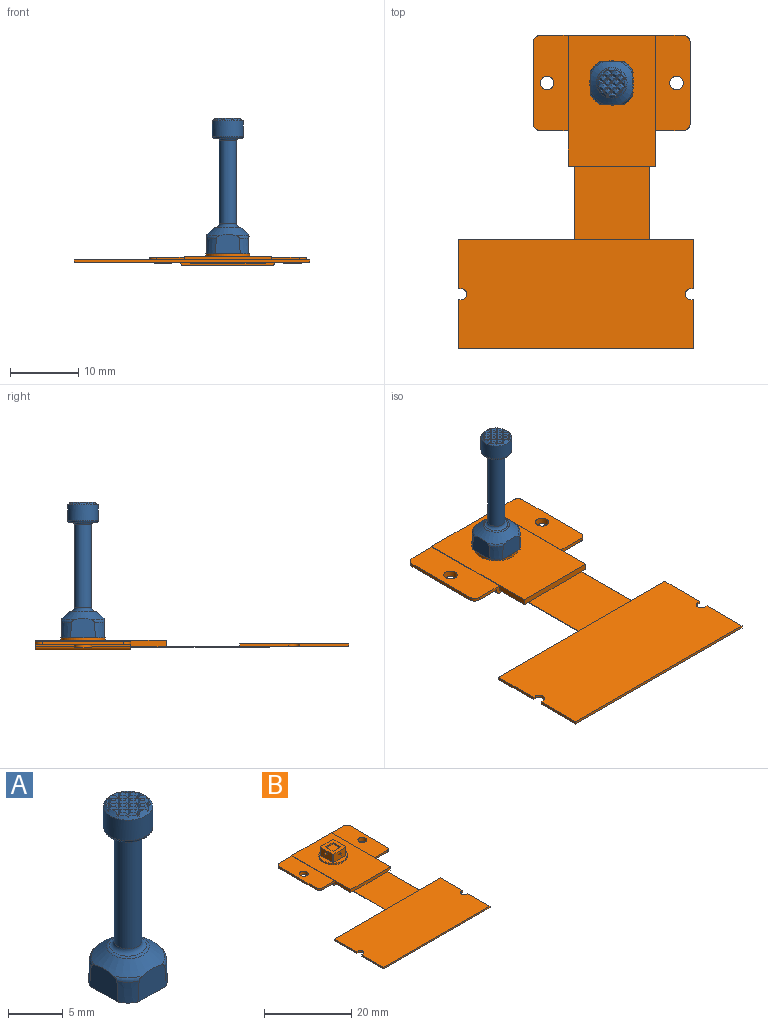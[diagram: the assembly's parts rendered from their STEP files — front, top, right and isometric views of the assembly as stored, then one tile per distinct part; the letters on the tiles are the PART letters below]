
ASSEMBLY  parts=2 mates=1
PART A: 159 faces, bbox 7.2x7.2x20 mm
  f0: plane 6.2x6.2mm, normal (0,0,-1), area 16mm2, adj f1,f2,f3,f4,f15,f16,f17,f18
  f1: cone r=3.51mm half-angle=2deg, axis (0,0,-1), area 4.4mm2, adj f0,f7,f154,f157
  f2: cone r=3.51mm half-angle=2deg, axis (0,0,-1), area 4.4mm2, adj f0,f6,f156,f157
  f3: cone r=3.51mm half-angle=2deg, axis (0,0,-1), area 4.4mm2, adj f0,f8,f155,f156
  f4: cone r=3.51mm half-angle=2deg, axis (0,0,-1), area 4.4mm2, adj f0,f32,f154,f155
  f5: cone r=1.8mm half-angle=50.7deg, axis (0,0,-1), area 27.9mm2, adj f6,f7,f8,f32,f33,f154,f155,f156
  f6: torus R=3.02mm, axis (0,0,1), area 1mm2, adj f2,f5,f156,f157
  f7: torus R=3.02mm, axis (0,0,1), area 1mm2, adj f1,f5,f154,f157
  f8: torus R=3.02mm, axis (0,0,1), area 1mm2, adj f3,f5,f155,f156
  f9: plane 0.42x0.22mm, normal (0,0,1), area 0mm2, adj f13,f52,f62
  f10: plane 0.42x0.22mm, normal (0,0,1), area 0mm2, adj f13,f55,f68
  f11: plane 0.42x0.22mm, normal (0,0,1), area 0mm2, adj f13,f87,f96
  f12: plane 0.42x0.22mm, normal (0,0,1), area 0mm2, adj f13,f129,f135
  f13: cone r=1.85mm half-angle=45deg, axis (0,0,-1), area 5.1mm2, adj f9,f10,f11,f12,f34,f36,f37,f38
  f14: cylinder r=1.25mm len=12.21mm, axis (0,0,-1), area 95.9mm2, adj f153,f158
  f15: plane 4.4x2.4mm, normal (1,0,0), area 9.7mm2, adj f0,f16,f18,f19,f29,f30,f31
  f16: plane 4.4x2.4mm, normal (0,-1,0), area 9.7mm2, adj f0,f15,f17,f19,f26,f27,f28
  f17: plane 4.4x2.4mm, normal (-1,0,0), area 9.7mm2, adj f0,f16,f18,f19,f23,f24,f25
  f18: plane 4.4x2.4mm, normal (0,1,0), area 9.7mm2, adj f0,f15,f17,f19,f20,f21,f22
  f19: plane 4.4x4.4mm, normal (0,0,-1), area 19.4mm2, adj f15,f16,f17,f18
  f20: plane 2x0.45mm, normal (-0.89,0.45,0), area 1mm2, adj f0,f18,f21,f22
  f21: plane 2x0.45mm, normal (0.89,0.45,0), area 1mm2, adj f0,f18,f20,f22
  f22: plane 0.45x0.45mm, normal (0,0,-1), area 0.1mm2, adj f18,f20,f21
  f23: plane 2x0.45mm, normal (-0.45,-0.89,0), area 1mm2, adj f0,f17,f24,f25
  f24: plane 2x0.45mm, normal (-0.45,0.89,0), area 1mm2, adj f0,f17,f23,f25
  f25: plane 0.45x0.45mm, normal (0,0,-1), area 0.1mm2, adj f17,f23,f24
  f26: plane 2x0.45mm, normal (0.89,-0.45,0), area 1mm2, adj f0,f16,f27,f28
  f27: plane 2x0.45mm, normal (-0.89,-0.45,0), area 1mm2, adj f0,f16,f26,f28
  f28: plane 0.45x0.45mm, normal (0,0,-1), area 0.1mm2, adj f16,f26,f27
  f29: plane 2x0.45mm, normal (0.45,0.89,0), area 1mm2, adj f0,f15,f30,f31
  f30: plane 2x0.45mm, normal (0.45,-0.89,0), area 1mm2, adj f0,f15,f29,f31
  f31: plane 0.45x0.45mm, normal (0,0,-1), area 0.1mm2, adj f15,f29,f30
  f32: torus R=3.02mm, axis (0,0,1), area 1mm2, adj f4,f5,f154,f155
  f33: torus R=1.62mm, axis (0,0,-1), area 3.2mm2, adj f5,f158
  f34: cylinder r=2.25mm len=4.5mm, axis (0,0,1), area 32.5mm2, adj f13,f152
  f35: plane 3.9x3.9mm, normal (0,0,-1), area 4.4mm2, adj f152,f153
  f36: plane 0.07x0.07mm, normal (0.5,0.5,0.71), area 0mm2, adj f13,f37,f42
  f37: plane 0.08x0.07mm, normal (-0.5,-0.5,0.71), area 0mm2, adj f13,f36,f44
  f38: plane 0.08x0.07mm, normal (0.5,0.5,0.71), area 0mm2, adj f13,f39,f46
  f39: plane 0.07x0.07mm, normal (-0.5,-0.5,0.71), area 0mm2, adj f13,f38,f48
  f40: plane 0.22x0.22mm, normal (-0.5,-0.5,0.71), area 0mm2, adj f13,f41,f46
  f41: plane 0.22x0.22mm, normal (0.5,0.5,0.71), area 0mm2, adj f13,f40,f44
  f42: plane 0.13x0.13mm, normal (-0.5,0.5,0.71), area 0mm2, adj f13,f36,f43
  f43: plane 0.2x0.14mm, normal (0.5,-0.5,0.71), area 0mm2, adj f13,f42,f52
  f44: plane 0.68x0.68mm, normal (-0.5,0.5,0.71), area 0.1mm2, adj f13,f37,f41,f45
  f45: plane 0.64x0.64mm, normal (0.5,-0.5,0.71), area 0.2mm2, adj f44,f53,f59,f151
  f46: plane 0.68x0.68mm, normal (-0.5,0.5,0.71), area 0.1mm2, adj f13,f38,f40,f47
  f47: plane 0.64x0.64mm, normal (0.5,-0.5,0.71), area 0.2mm2, adj f46,f54,f58,f150
  f48: plane 0.13x0.13mm, normal (-0.5,0.5,0.71), area 0mm2, adj f13,f39,f49
  f49: plane 0.2x0.14mm, normal (0.5,-0.5,0.71), area 0mm2, adj f13,f48,f55
  f50: plane 0.13x0.13mm, normal (0.5,0.5,0.71), area 0mm2, adj f13,f51,f60
  f51: plane 0.2x0.14mm, normal (-0.5,-0.5,0.71), area 0mm2, adj f13,f50,f62
  f52: plane 0.64x0.64mm, normal (0.5,0.5,0.71), area 0.2mm2, adj f9,f13,f43,f53,f62
  f53: plane 0.64x0.64mm, normal (-0.5,-0.5,0.71), area 0.2mm2, adj f45,f52,f64,f151
  f54: plane 0.64x0.64mm, normal (0.5,0.5,0.71), area 0.2mm2, adj f47,f55,f66,f150
  f55: plane 0.64x0.64mm, normal (-0.5,-0.5,0.71), area 0.2mm2, adj f10,f13,f49,f54,f68
  f56: plane 0.2x0.14mm, normal (0.5,0.5,0.71), area 0mm2, adj f13,f57,f68
  f57: plane 0.13x0.13mm, normal (-0.5,-0.5,0.71), area 0mm2, adj f13,f56,f70
  f58: plane 0.64x0.64mm, normal (-0.5,-0.5,0.71), area 0.2mm2, adj f47,f59,f66,f150
  f59: plane 0.64x0.64mm, normal (0.5,0.5,0.71), area 0.2mm2, adj f45,f58,f64,f151
  f60: plane 0.07x0.07mm, normal (-0.5,0.5,0.71), area 0mm2, adj f13,f50,f61
  f61: plane 0.08x0.07mm, normal (0.5,-0.5,0.71), area 0mm2, adj f13,f60,f72
  f62: plane 0.64x0.64mm, normal (-0.5,0.5,0.71), area 0.2mm2, adj f9,f13,f51,f52,f63
  f63: plane 0.64x0.64mm, normal (0.5,-0.5,0.71), area 0.2mm2, adj f62,f73,f74,f147
  f64: plane 0.64x0.64mm, normal (-0.5,0.5,0.71), area 0.2mm2, adj f53,f59,f65,f151
  f65: plane 0.64x0.64mm, normal (0.5,-0.5,0.71), area 0.2mm2, adj f64,f75,f81,f145
  f66: plane 0.64x0.64mm, normal (-0.5,0.5,0.71), area 0.2mm2, adj f54,f58,f67,f150
  f67: plane 0.64x0.64mm, normal (0.5,-0.5,0.71), area 0.2mm2, adj f66,f76,f80,f144
  f68: plane 0.64x0.64mm, normal (-0.5,0.5,0.71), area 0.2mm2, adj f10,f13,f55,f56,f69
  f69: plane 0.64x0.64mm, normal (0.5,-0.5,0.71), area 0.2mm2, adj f68,f77,f78,f143
  f70: plane 0.07x0.07mm, normal (-0.5,0.5,0.71), area 0mm2, adj f13,f57,f71
  f71: plane 0.08x0.07mm, normal (0.5,-0.5,0.71), area 0mm2, adj f13,f70,f79
  f72: plane 0.68x0.68mm, normal (0.5,0.5,0.71), area 0.1mm2, adj f13,f61,f73,f113
  f73: plane 0.64x0.64mm, normal (-0.5,-0.5,0.71), area 0.2mm2, adj f63,f72,f115,f147
  f74: plane 0.64x0.64mm, normal (0.5,0.5,0.71), area 0.2mm2, adj f63,f75,f115,f147
  f75: plane 0.64x0.64mm, normal (-0.5,-0.5,0.71), area 0.2mm2, adj f65,f74,f117,f145
  f76: plane 0.64x0.64mm, normal (0.5,0.5,0.71), area 0.2mm2, adj f67,f77,f119,f144
  f77: plane 0.64x0.64mm, normal (-0.5,-0.5,0.71), area 0.2mm2, adj f69,f76,f121,f143
  f78: plane 0.64x0.64mm, normal (0.5,0.5,0.71), area 0.2mm2, adj f69,f79,f121,f143
  f79: plane 0.68x0.68mm, normal (-0.5,-0.5,0.71), area 0.1mm2, adj f13,f71,f78,f123
  f80: plane 0.64x0.64mm, normal (-0.5,-0.5,0.71), area 0.2mm2, adj f67,f81,f119,f144
  f81: plane 0.64x0.64mm, normal (0.5,0.5,0.71), area 0.2mm2, adj f65,f80,f117,f145
  f82: plane 0.08x0.07mm, normal (-0.5,0.5,0.71), area 0mm2, adj f13,f83,f84
  f83: plane 0.07x0.07mm, normal (0.5,-0.5,0.71), area 0mm2, adj f13,f82,f94
  f84: plane 0.68x0.68mm, normal (0.5,0.5,0.71), area 0.1mm2, adj f13,f82,f85,f112
  f85: plane 0.64x0.64mm, normal (-0.5,-0.5,0.71), area 0.2mm2, adj f84,f86,f114,f148
  f86: plane 0.64x0.64mm, normal (-0.5,0.5,0.71), area 0.2mm2, adj f85,f87,f88,f148
  f87: plane 0.64x0.64mm, normal (0.5,-0.5,0.71), area 0.2mm2, adj f11,f13,f86,f95,f96
  f88: plane 0.64x0.64mm, normal (0.5,0.5,0.71), area 0.2mm2, adj f86,f89,f114,f148
  f89: plane 0.64x0.64mm, normal (-0.5,-0.5,0.71), area 0.2mm2, adj f88,f90,f116,f146
  f90: plane 0.64x0.64mm, normal (-0.5,0.5,0.71), area 0.2mm2, adj f89,f91,f93,f146
  f91: plane 0.64x0.64mm, normal (0.5,-0.5,0.71), area 0.2mm2, adj f90,f97,f99,f149
  f92: plane 0.64x0.64mm, normal (-0.5,-0.5,0.71), area 0.2mm2, adj f93,f118,f126,f142
  f93: plane 0.64x0.64mm, normal (0.5,0.5,0.71), area 0.2mm2, adj f90,f92,f116,f146
  f94: plane 0.13x0.13mm, normal (0.5,0.5,0.71), area 0mm2, adj f13,f83,f95
  f95: plane 0.2x0.14mm, normal (-0.5,-0.5,0.71), area 0mm2, adj f13,f87,f94
  f96: plane 0.64x0.64mm, normal (0.5,0.5,0.71), area 0.2mm2, adj f11,f13,f87,f97,f100
  f97: plane 0.64x0.64mm, normal (-0.5,-0.5,0.71), area 0.2mm2, adj f91,f96,f102,f149
  f98: plane 0.64x0.64mm, normal (-0.5,-0.5,0.71), area 0.2mm2, adj f99,f104,f127,f140
  f99: plane 0.64x0.64mm, normal (0.5,0.5,0.71), area 0.2mm2, adj f91,f98,f102,f149
  f100: plane 0.2x0.14mm, normal (-0.5,0.5,0.71), area 0mm2, adj f13,f96,f101
  f101: plane 0.13x0.13mm, normal (0.5,-0.5,0.71), area 0mm2, adj f13,f100,f106
  f102: plane 0.64x0.64mm, normal (-0.5,0.5,0.71), area 0.2mm2, adj f97,f99,f103,f149
  f103: plane 0.68x0.68mm, normal (0.5,-0.5,0.71), area 0.1mm2, adj f13,f102,f107,f111
  f104: plane 0.64x0.64mm, normal (-0.5,0.5,0.71), area 0.2mm2, adj f98,f105,f134,f140
  f105: plane 0.68x0.68mm, normal (0.5,-0.5,0.71), area 0.1mm2, adj f13,f104,f108,f110
  f106: plane 0.07x0.07mm, normal (0.5,0.5,0.71), area 0mm2, adj f13,f101,f107
  f107: plane 0.08x0.07mm, normal (-0.5,-0.5,0.71), area 0mm2, adj f13,f103,f106
  f108: plane 0.08x0.07mm, normal (0.5,0.5,0.71), area 0mm2, adj f13,f105,f109
  f109: plane 0.07x0.07mm, normal (-0.5,-0.5,0.71), area 0mm2, adj f13,f108,f139
  f110: plane 0.22x0.22mm, normal (-0.5,-0.5,0.71), area 0mm2, adj f13,f105,f111
  f111: plane 0.22x0.22mm, normal (0.5,0.5,0.71), area 0mm2, adj f13,f103,f110
  f112: plane 0.22x0.22mm, normal (0.5,-0.5,0.71), area 0mm2, adj f13,f84,f113
  f113: plane 0.22x0.22mm, normal (-0.5,0.5,0.71), area 0mm2, adj f13,f72,f112
  f114: plane 0.64x0.64mm, normal (0.5,-0.5,0.71), area 0.2mm2, adj f85,f88,f115,f148
  f115: plane 0.64x0.64mm, normal (-0.5,0.5,0.71), area 0.2mm2, adj f73,f74,f114,f147
  f116: plane 0.64x0.64mm, normal (0.5,-0.5,0.71), area 0.2mm2, adj f89,f93,f117,f146
  f117: plane 0.64x0.64mm, normal (-0.5,0.5,0.71), area 0.2mm2, adj f75,f81,f116,f145
  f118: plane 0.64x0.64mm, normal (0.5,-0.5,0.71), area 0.2mm2, adj f92,f119,f124,f142
  f119: plane 0.64x0.64mm, normal (-0.5,0.5,0.71), area 0.2mm2, adj f76,f80,f118,f144
  f120: plane 0.64x0.64mm, normal (0.5,-0.5,0.71), area 0.2mm2, adj f121,f125,f130,f141
  f121: plane 0.64x0.64mm, normal (-0.5,0.5,0.71), area 0.2mm2, adj f77,f78,f120,f143
  f122: plane 0.22x0.22mm, normal (0.5,-0.5,0.71), area 0mm2, adj f13,f123,f131
  f123: plane 0.22x0.22mm, normal (-0.5,0.5,0.71), area 0mm2, adj f13,f79,f122
  f124: plane 0.64x0.64mm, normal (0.5,0.5,0.71), area 0.2mm2, adj f118,f125,f126,f142
  f125: plane 0.64x0.64mm, normal (-0.5,-0.5,0.71), area 0.2mm2, adj f120,f124,f128,f141
  f126: plane 0.64x0.64mm, normal (-0.5,0.5,0.71), area 0.2mm2, adj f92,f124,f127,f142
  f127: plane 0.64x0.64mm, normal (0.5,-0.5,0.71), area 0.2mm2, adj f98,f126,f134,f140
  f128: plane 0.64x0.64mm, normal (-0.5,0.5,0.71), area 0.2mm2, adj f125,f129,f130,f141
  f129: plane 0.64x0.64mm, normal (0.5,-0.5,0.71), area 0.2mm2, adj f12,f13,f128,f135,f136
  f130: plane 0.64x0.64mm, normal (0.5,0.5,0.71), area 0.2mm2, adj f120,f128,f131,f141
  f131: plane 0.68x0.68mm, normal (-0.5,-0.5,0.71), area 0.1mm2, adj f13,f122,f130,f132
  f132: plane 0.08x0.07mm, normal (-0.5,0.5,0.71), area 0mm2, adj f13,f131,f133
  f133: plane 0.07x0.07mm, normal (0.5,-0.5,0.71), area 0mm2, adj f13,f132,f137
  f134: plane 0.64x0.64mm, normal (0.5,0.5,0.71), area 0.2mm2, adj f104,f127,f135,f140
  f135: plane 0.64x0.64mm, normal (-0.5,-0.5,0.71), area 0.2mm2, adj f12,f13,f129,f134,f138
  f136: plane 0.2x0.14mm, normal (0.5,0.5,0.71), area 0mm2, adj f13,f129,f137
  f137: plane 0.13x0.13mm, normal (-0.5,-0.5,0.71), area 0mm2, adj f13,f133,f136
  f138: plane 0.2x0.14mm, normal (-0.5,0.5,0.71), area 0mm2, adj f13,f135,f139
  f139: plane 0.13x0.13mm, normal (0.5,-0.5,0.71), area 0mm2, adj f13,f109,f138
  f140: plane 0.57x0.57mm, normal (0,0,1), area 0.2mm2, adj f98,f104,f127,f134
  f141: plane 0.57x0.57mm, normal (0,0,1), area 0.2mm2, adj f120,f125,f128,f130
  f142: plane 0.57x0.57mm, normal (0,0,1), area 0.2mm2, adj f92,f118,f124,f126
  f143: plane 0.57x0.57mm, normal (0,0,1), area 0.2mm2, adj f69,f77,f78,f121
  f144: plane 0.57x0.57mm, normal (0,0,1), area 0.2mm2, adj f67,f76,f80,f119
  f145: plane 0.57x0.57mm, normal (0,0,1), area 0.2mm2, adj f65,f75,f81,f117
  f146: plane 0.57x0.57mm, normal (0,0,1), area 0.2mm2, adj f89,f90,f93,f116
  f147: plane 0.57x0.57mm, normal (0,0,1), area 0.2mm2, adj f63,f73,f74,f115
  f148: plane 0.57x0.57mm, normal (0,0,1), area 0.2mm2, adj f85,f86,f88,f114
  f149: plane 0.57x0.57mm, normal (0,0,1), area 0.2mm2, adj f91,f97,f99,f102
  f150: plane 0.57x0.57mm, normal (0,0,1), area 0.2mm2, adj f47,f54,f58,f66
  f151: plane 0.57x0.57mm, normal (0,0,1), area 0.2mm2, adj f45,f53,f59,f64
  f152: torus R=1.95mm, axis (0,0,1), area 6.3mm2, adj f34,f35
  f153: torus R=1.55mm, axis (0,0,1), area 4mm2, adj f14,f35
  f154: plane 3.81x2.99mm, normal (-1,0,0), area 9.4mm2, adj f0,f1,f4,f5,f7,f32
  f155: plane 3.81x2.99mm, normal (0,1,0), area 9.4mm2, adj f0,f3,f4,f5,f8,f32
  f156: plane 3.81x2.99mm, normal (1,0,0), area 9.4mm2, adj f0,f2,f3,f5,f6,f8
  f157: plane 3.81x2.99mm, normal (0,-1,0), area 9.4mm2, adj f0,f1,f2,f5,f6,f7
  f158: torus R=1.75mm, axis (0,0,1), area 6.4mm2, adj f14,f33
PART B: 80 faces, bbox 34.5x46x4.1 mm
  f0: plane 5.2x0.9mm, normal (0,0,-1), area 4.7mm2, adj f11,f28,f30,f76
  f1: plane 4.3x4.3mm, normal (0,0,1), area 12.1mm2, adj f2,f3,f34,f35,f36,f37,f38,f39
  f2: plane 3.8x2.3mm, normal (1,0,0), area 8.5mm2, adj f1,f4,f36,f38,f48,f49,f50,f51
  f3: plane 3.8x2.3mm, normal (0,-1,0), area 8.5mm2, adj f1,f4,f38,f39,f44,f45,f46,f47
  f4: plane 6.5x6.5mm, normal (0,0,1), area 14.8mm2, adj f2,f3,f33,f34,f35,f36,f37,f38
  f5: plane 14x4.6mm, normal (0,0,-1), area 58.7mm2, adj f8,f9,f11,f12,f14,f16,f17
  f6: plane 14x12.8mm, normal (0,0,-1), area 179.2mm2, adj f7,f11,f12,f19
  f7: cylinder r=0.5mm len=14mm, axis (0,1,0), area 11mm2, adj f6,f8,f11,f12
  f8: plane 14x0.3mm, normal (1,0,0), area 4.2mm2, adj f5,f7,f11,f12
  f9: plane 12x0.5mm, normal (1,0,0), area 6mm2, adj f5,f10,f16,f17
  f10: plane 14x5.1mm, normal (0,0,1), area 67.8mm2, adj f9,f11,f12,f13,f16,f17,f29
  f11: plane 21x1.3mm, normal (0,-1,0), area 10.1mm2, adj f0,f5,f6,f7,f8,f10,f17,f18
  f12: plane 21x1.4mm, normal (0,1,0), area 22.7mm2, adj f5,f6,f7,f8,f10,f16,f18,f19
  f13: cylinder r=1mm len=2mm, axis (0,0,1), area 6.3mm2, adj f10,f15
  f14: cylinder r=1.3mm len=2.6mm, axis (0,0,1), area 4.1mm2, adj f5,f15
  f15: plane 2.6x2.6mm, normal (0,0,-1), area 2.2mm2, adj f13,f14
  f16: cylinder r=1mm len=1mm, axis (0,0,1), area 0.8mm2, adj f5,f9,f10,f12
  f17: cylinder r=1mm len=1mm, axis (0,0,-1), area 0.8mm2, adj f5,f9,f10,f11
  f18: plane 14x4.6mm, normal (0,0,-1), area 58.7mm2, adj f11,f12,f20,f21,f24,f26,f27
  f19: cylinder r=0.5mm len=14mm, axis (0,1,0), area 11mm2, adj f6,f11,f12,f20
  f20: plane 14x0.3mm, normal (-1,0,0), area 4.2mm2, adj f11,f12,f18,f19
  f21: plane 12x0.5mm, normal (-1,0,0), area 6mm2, adj f18,f22,f26,f27
  f22: plane 14x5.1mm, normal (0,0,1), area 67.8mm2, adj f11,f12,f21,f23,f26,f27,f28
  f23: cylinder r=1mm len=2mm, axis (0,0,1), area 6.3mm2, adj f22,f25
  f24: cylinder r=1.3mm len=2.6mm, axis (0,0,1), area 4.1mm2, adj f18,f25
  f25: plane 2.6x2.6mm, normal (0,0,-1), area 2.2mm2, adj f23,f24
  f26: cylinder r=1mm len=1mm, axis (0,0,1), area 0.8mm2, adj f12,f18,f21,f22
  f27: cylinder r=1mm len=1mm, axis (0,0,-1), area 0.8mm2, adj f11,f18,f21,f22
  f28: plane 19.2x0.9mm, normal (-1,0,0), area 6.1mm2, adj f0,f11,f12,f22,f30,f31
  f29: plane 19.2x0.9mm, normal (1,0,0), area 6.1mm2, adj f10,f11,f12,f30,f31,f32
  f30: plane 12.8x0.9mm, normal (0,-1,0), area 11.5mm2, adj f0,f28,f29,f31,f32,f79
  f31: plane 19.2x12.8mm, normal (0,0,1), area 212.6mm2, adj f12,f28,f29,f30,f33
  f32: plane 5.2x0.9mm, normal (0,0,-1), area 4.7mm2, adj f11,f29,f30,f77
  f33: cylinder r=3.25mm len=6.5mm, axis (0,0,-1), area 8.2mm2, adj f4,f31
  f34: plane 3.8x2.3mm, normal (0,1,0), area 8.5mm2, adj f1,f4,f36,f37,f52,f53,f54,f55
  f35: plane 3.8x2.3mm, normal (-1,0,0), area 8.5mm2, adj f1,f4,f37,f39,f40,f41,f42,f43
  f36: plane 2.3x0.25mm, normal (0.71,0.71,0), area 0.8mm2, adj f1,f2,f4,f34
  f37: plane 2.3x0.25mm, normal (-0.71,0.71,0), area 0.8mm2, adj f1,f4,f34,f35
  f38: plane 2.3x0.25mm, normal (0.71,-0.71,0), area 0.8mm2, adj f1,f2,f3,f4
  f39: plane 2.3x0.25mm, normal (-0.71,-0.71,0), area 0.8mm2, adj f1,f3,f4,f35
  f40: plane 0.5x0.5mm, normal (-0.45,-0.89,0), area 0.3mm2, adj f35,f41,f42,f43
  f41: plane 0.5x0.5mm, normal (-0.45,0.89,0), area 0.3mm2, adj f35,f40,f42,f43
  f42: plane 0.5x0.5mm, normal (0,0,-1), area 0.1mm2, adj f35,f40,f41
  f43: plane 0.5x0.5mm, normal (-0.17,0,0.98), area 0.1mm2, adj f35,f40,f41
  f44: plane 0.5x0.5mm, normal (0.89,-0.45,0), area 0.3mm2, adj f3,f45,f46,f47
  f45: plane 0.5x0.5mm, normal (-0.89,-0.45,0), area 0.3mm2, adj f3,f44,f46,f47
  f46: plane 0.5x0.5mm, normal (0,0,-1), area 0.1mm2, adj f3,f44,f45
  f47: plane 0.5x0.5mm, normal (0,-0.17,0.98), area 0.1mm2, adj f3,f44,f45
  f48: plane 0.5x0.5mm, normal (0.45,0.89,0), area 0.3mm2, adj f2,f49,f50,f51
  f49: plane 0.5x0.5mm, normal (0.45,-0.89,0), area 0.3mm2, adj f2,f48,f50,f51
  f50: plane 0.5x0.5mm, normal (0,0,-1), area 0.1mm2, adj f2,f48,f49
  f51: plane 0.5x0.5mm, normal (0.17,0,0.98), area 0.1mm2, adj f2,f48,f49
  f52: plane 0.5x0.5mm, normal (-0.89,0.45,0), area 0.3mm2, adj f34,f53,f54,f55
  f53: plane 0.5x0.5mm, normal (0.89,0.45,0), area 0.3mm2, adj f34,f52,f54,f55
  f54: plane 0.5x0.5mm, normal (0,0,-1), area 0.1mm2, adj f34,f52,f53
  f55: plane 0.5x0.5mm, normal (0,0.17,0.98), area 0.1mm2, adj f34,f52,f53
  f56: plane 2.5x0.4mm, normal (0,1,0), area 1mm2, adj f1,f57,f59,f60
  f57: plane 2.5x0.4mm, normal (-1,0,0), area 1mm2, adj f1,f56,f58,f60
  f58: plane 2.5x0.4mm, normal (0,-1,0), area 1mm2, adj f1,f57,f59,f60
  f59: plane 2.5x0.4mm, normal (1,0,0), area 1mm2, adj f1,f56,f58,f60
  f60: plane 2.5x2.5mm, normal (0,0,1), area 6.2mm2, adj f56,f57,f58,f59
  f61: plane 7.2x0.4mm, normal (1,0,0), area 2.9mm2, adj f63,f64,f68,f71
  f62: plane 7.2x0.4mm, normal (-1,0,0), area 2.9mm2, adj f63,f64,f68,f72
  f63: plane 34.5x16mm, normal (0,0,1), area 548.7mm2, adj f61,f62,f64,f65,f66,f67,f69,f70
  f64: plane 34.5x0.4mm, normal (0,-1,0), area 13.8mm2, adj f61,f62,f63,f68
  f65: plane 7.2x0.4mm, normal (1,0,0), area 2.9mm2, adj f63,f66,f68,f69
  f66: plane 34.5x0.4mm, normal (0,1,0), area 13.8mm2, adj f63,f65,f67,f68,f79
  f67: plane 7.2x0.4mm, normal (-1,0,0), area 2.9mm2, adj f63,f66,f68,f74
  f68: plane 34.5x16mm, normal (0,0,-1), area 500.8mm2, adj f61,f62,f64,f65,f66,f67,f69,f70
  f69: plane 0.4x0.4mm, normal (0,-1,0), area 0.2mm2, adj f63,f65,f68,f70
  f70: cylinder r=0.8mm len=1.6mm, axis (0,0,1), area 1mm2, adj f63,f68,f69,f71
  f71: plane 0.4x0.4mm, normal (0,1,0), area 0.2mm2, adj f61,f63,f68,f70
  f72: plane 0.4x0.4mm, normal (0,1,0), area 0.2mm2, adj f62,f63,f68,f73
  f73: cylinder r=0.8mm len=1.6mm, axis (0,0,1), area 1mm2, adj f63,f68,f72,f74
  f74: plane 0.4x0.4mm, normal (0,-1,0), area 0.2mm2, adj f63,f67,f68,f73
  f75: plane 11x0.1mm, normal (0,-1,0), area 1.1mm2, adj f68,f76,f77,f78
  f76: plane 20.36x0.1mm, normal (-1,0,0), area 2mm2, adj f0,f11,f68,f75,f78,f79
  f77: plane 20.36x0.1mm, normal (1,0,0), area 2mm2, adj f11,f32,f68,f75,f78,f79
  f78: plane 20.36x11mm, normal (0,0,-1), area 223.9mm2, adj f11,f75,f76,f77
  f79: plane 11x10.8mm, normal (0,0,1), area 118.8mm2, adj f30,f66,f76,f77
PLACE A t=(3.44,19.35,7.03)mm
PLACE B t=(3.44,19.35,7.03)mm
MATE fastened B.f33 <-> A.f1  axis (0,0,1) through (3.44,19.35,7.53)mm
